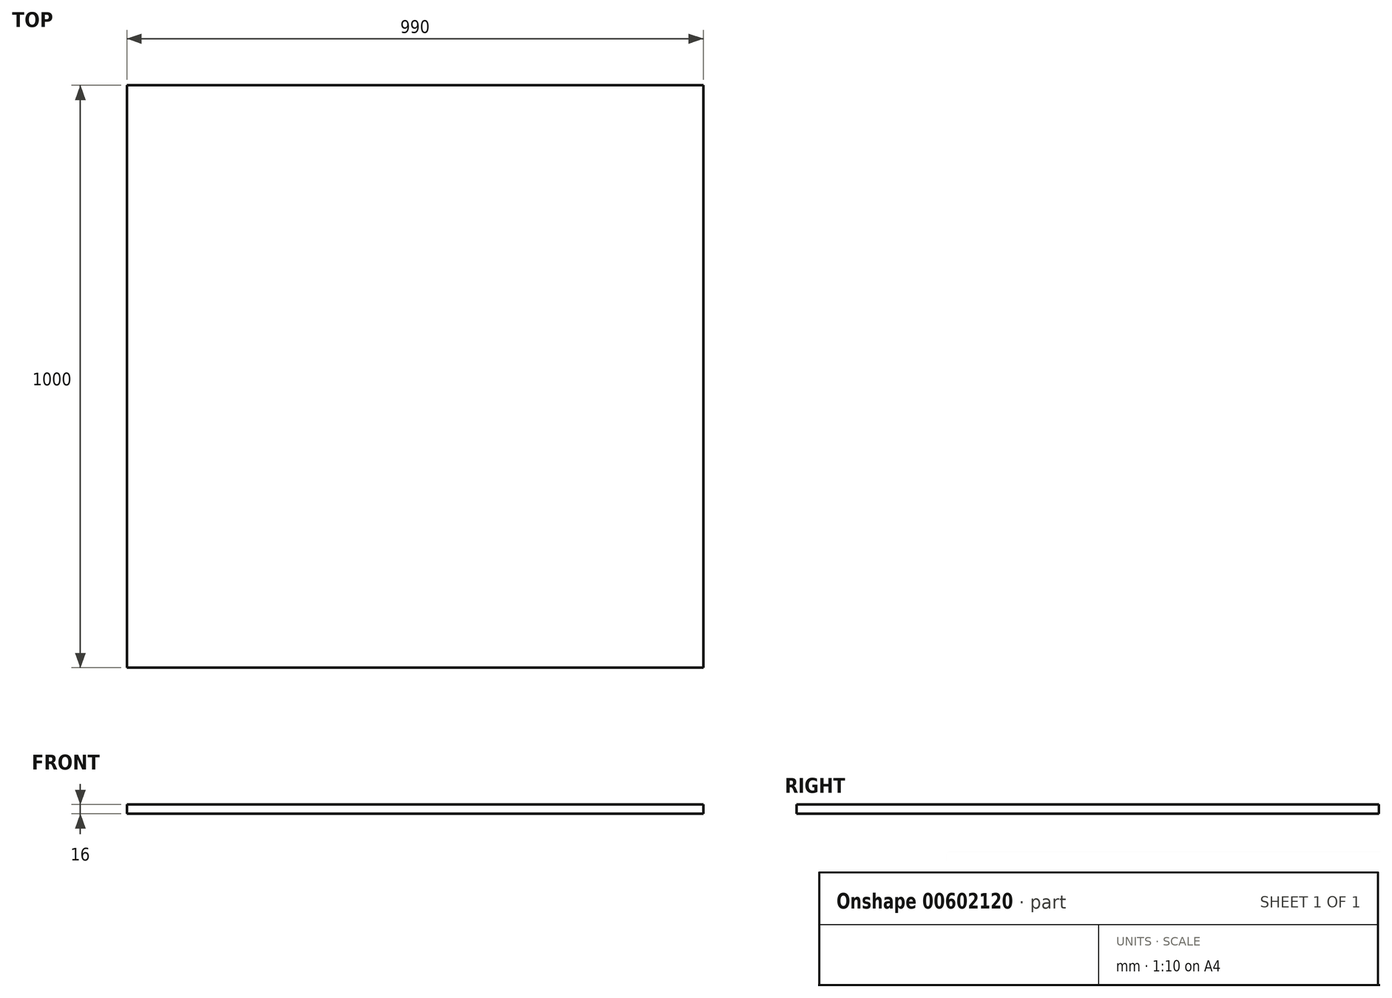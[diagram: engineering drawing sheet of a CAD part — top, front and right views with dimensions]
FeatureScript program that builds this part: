
annotation { "Feature Type Name" : "Feature", "Feature Type Description" : "" }
export const myFeature = defineFeature(function(context is Context, id is Id, definition is map)
    precondition{}
    {
        {
            var Q0;
            Q0=qCreatedBy(makeId("Top.planeOp"),FACE);
            var sketch = newSketch(context, id + "F0", { "sketchPlane" : qUnion([Q0])});
            skLineSegment(sketch, "E0.bottom", {"start": v(0, 0) * mm, "end": v(990, 0) * mm});
            skLineSegment(sketch, "E0.top", {"start": v(0, -1000) * mm, "end": v(990, -1000) * mm});
            skLineSegment(sketch, "E0.left", {"start": v(0, 0) * mm, "end": v(0, -1000) * mm});
            skLineSegment(sketch, "E0.right", {"start": v(990, 0) * mm, "end": v(990, -1000) * mm});
            skSolve(sketch);
        }
        {
            var Q0;
            Q0 = qSketchRegion(id + "F0", true);
            extrude(context, id + "F1", {"entities" : qUnion([Q0]), "depth" : 16 * mm, "offsetDistance" : 25 * mm});
        }
    });
